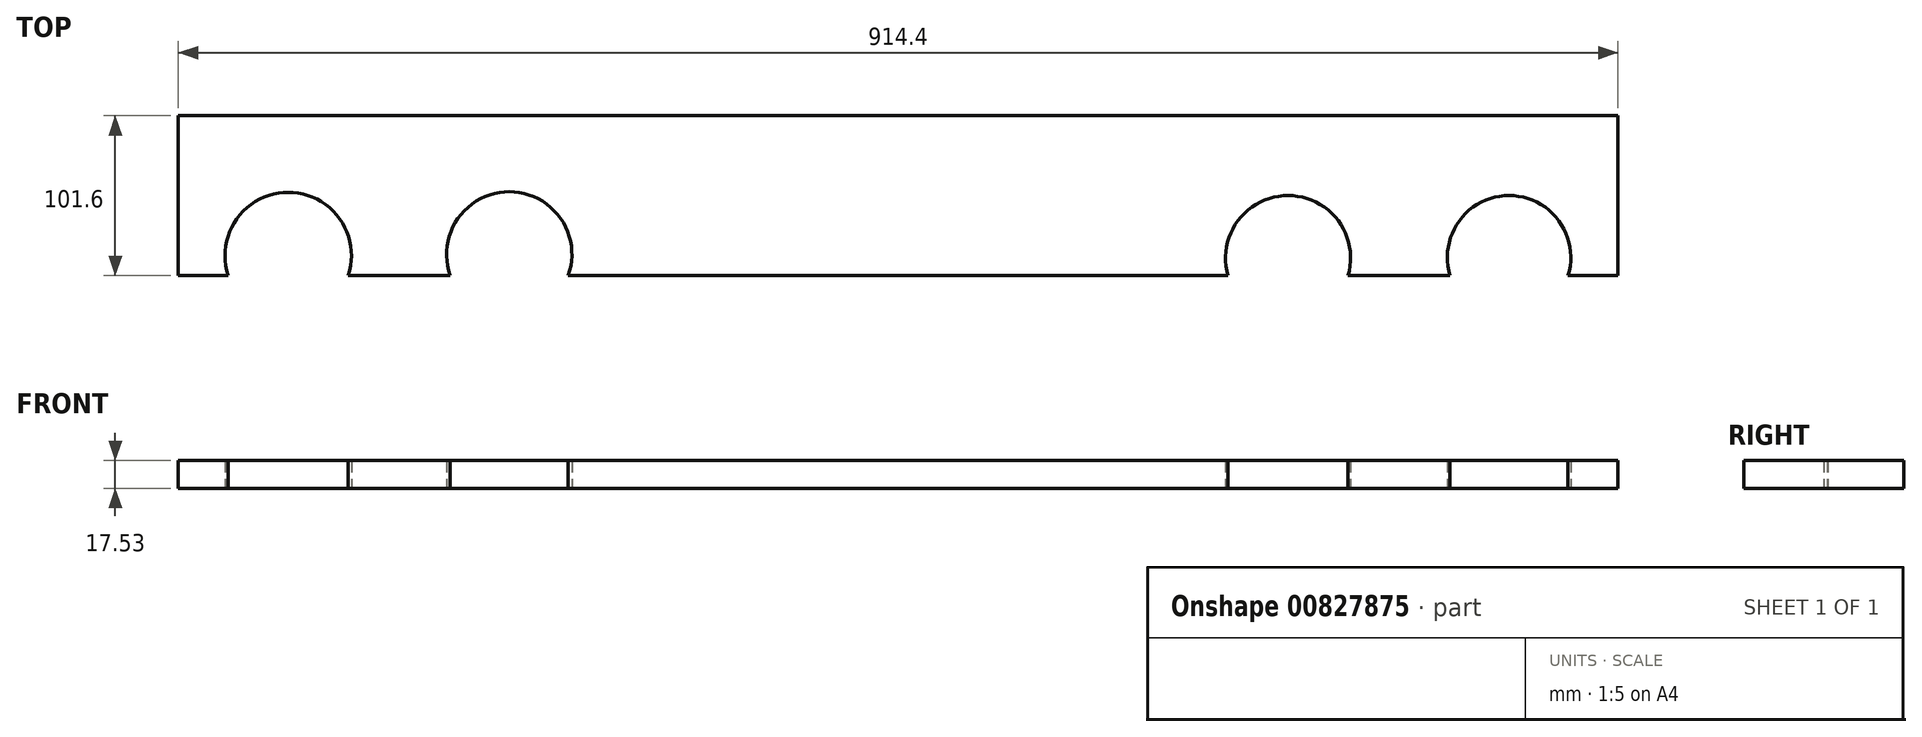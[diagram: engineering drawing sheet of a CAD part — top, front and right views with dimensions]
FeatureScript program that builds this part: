
annotation { "Feature Type Name" : "Feature", "Feature Type Description" : "" }
export const myFeature = defineFeature(function(context is Context, id is Id, definition is map)
    precondition{}
    {
        {
            var Q0;
            Q0=qCreatedBy(makeId("Top.planeOp"),FACE);
            var sketch = newSketch(context, id + "F0", { "sketchPlane" : qUnion([Q0])});
            skLineSegment(sketch, "E0.bottom", {"start": v(-457.2, 50.8) * mm, "end": v(457.2, 50.8) * mm});
            skLineSegment(sketch, "E0.top", {"start": v(-457.2, -50.8) * mm, "end": v(457.2, -50.8) * mm});
            skLineSegment(sketch, "E0.left", {"start": v(-457.2, 50.8) * mm, "end": v(-457.2, -50.8) * mm});
            skLineSegment(sketch, "E0.right", {"start": v(457.2, 50.8) * mm, "end": v(457.2, -50.8) * mm});
            skPoint(sketch, "E0.middle", {"position": v(0, 0) * mm});
            skPoint(sketch, "E1", {"position": v(-387.35, 0) * mm});
            skPoint(sketch, "E2", {"position": v(-247.65, 0) * mm});
            skPoint(sketch, "E3", {"position": v(247.65, 0) * mm});
            skPoint(sketch, "E4", {"position": v(387.35, 0) * mm});
            skArc(sketch, "E5", {"start": v(-349.25, -50.8) * mm, "mid": v(-387.35, 2.1) * mm, "end": v(-425.45, -50.8) * mm});
            skLineSegment(sketch, "E6", {"start": v(-387.35, 0) * mm, "end": v(-387.35, -50.8) * mm, "construction": true});
            skLineSegment(sketch, "E7", {"start": v(-247.65, 0) * mm, "end": v(-247.65, -50.8) * mm, "construction": true});
            skLineSegment(sketch, "E8", {"start": v(247.65, 0) * mm, "end": v(247.65, -50.8) * mm, "construction": true});
            skLineSegment(sketch, "E9", {"start": v(387.35, 0) * mm, "end": v(387.35, -50.8) * mm, "construction": true});
            skArc(sketch, "E10", {"start": v(-209.55, -50.8) * mm, "mid": v(-246.98, 2.49) * mm, "end": v(-284.42, -50.8) * mm});
            skPoint(sketch, "E11", {"position": v(209.55, -50.8) * mm});
            skPoint(sketch, "E12", {"position": v(350.6, -50.8) * mm});
            skPoint(sketch, "E13", {"position": v(247.65, -50.8) * mm});
            skPoint(sketch, "E14", {"position": v(285.75, -50.8) * mm});
            skPoint(sketch, "E15", {"position": v(425.45, -50.8) * mm});
            skArc(sketch, "E16", {"start": v(285.75, -50.8) * mm, "mid": v(247.65, 0.06) * mm, "end": v(209.55, -50.8) * mm});
            skArc(sketch, "E17", {"start": v(425.45, -50.8) * mm, "mid": v(388.02, 0.04) * mm, "end": v(350.6, -50.8) * mm});
            skSolve(sketch);
        }
        {
            var Q0;
            Q0=makeQuery(id+"F0.imprint","IMPRINT",FACE,{"disambiguationData":[TD([[makeQuery(id+"F0.imprint","IMPRINT",EDGE,{"derivedFrom":sQuery(id+"F0.wireOp",EDGE,"E0.bottom")}),-1.0]])]});
            extrude(context, id + "F1", {"entities" : qUnion([Q0]), "depth" : 17.53 * mm, "offsetDistance" : 25.4 * mm});
        }
    });
